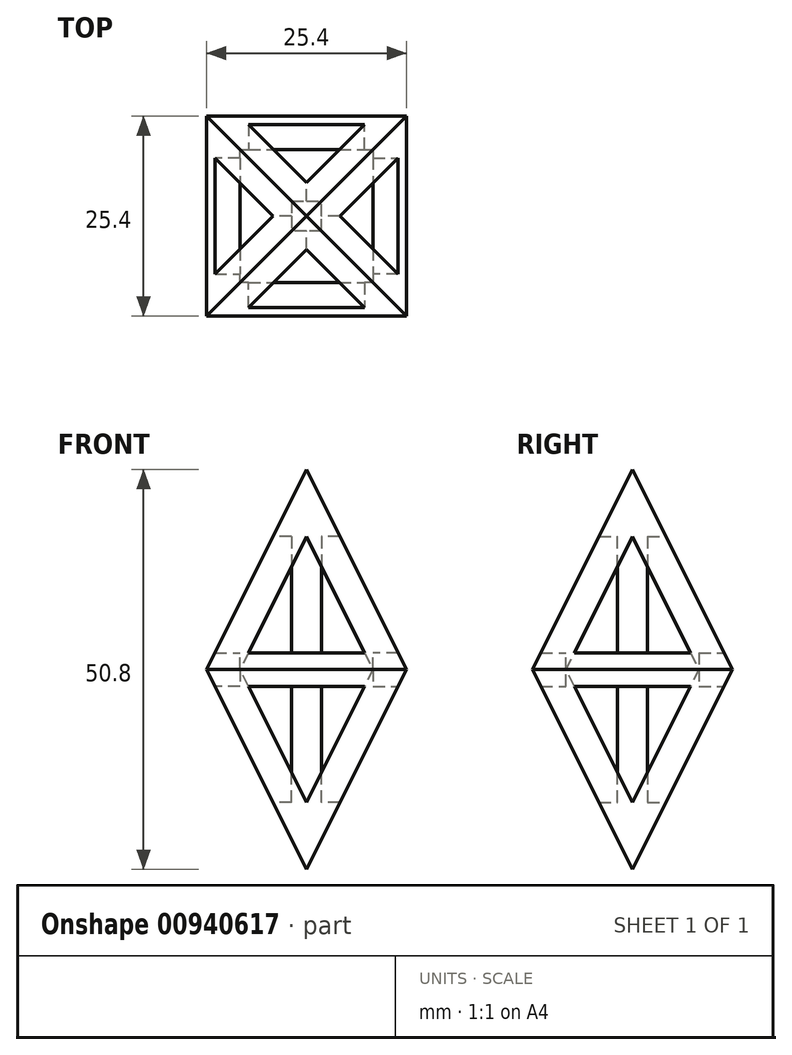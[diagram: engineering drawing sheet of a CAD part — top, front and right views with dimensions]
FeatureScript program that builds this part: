
annotation { "Feature Type Name" : "Feature", "Feature Type Description" : "" }
export const myFeature = defineFeature(function(context is Context, id is Id, definition is map)
    precondition{}
    {
        {
            var Q0;
            Q0=qCreatedBy(makeId("Right.planeOp"),FACE);
            var sketch = newSketch(context, id + "F0", { "sketchPlane" : qUnion([Q0])});
            skLineSegment(sketch, "E0.bottom", {"start": v(12.7, -25.4) * mm, "end": v(-12.7, -25.4) * mm});
            skLineSegment(sketch, "E0.top", {"start": v(12.7, 25.4) * mm, "end": v(-12.7, 25.4) * mm});
            skLineSegment(sketch, "E0.left", {"start": v(12.7, -25.4) * mm, "end": v(12.7, 25.4) * mm});
            skLineSegment(sketch, "E0.right", {"start": v(-12.7, -25.4) * mm, "end": v(-12.7, 25.4) * mm});
            skPoint(sketch, "E0.middle", {"position": v(0, 0) * mm});
            skSolve(sketch);
        }
        {
            var Q0;
            Q0=makeQuery(id+"F0.imprint","IMPRINT",FACE,{"disambiguationData":[TD([[makeQuery(id+"F0.imprint","IMPRINT",EDGE,{"derivedFrom":sQuery(id+"F0.wireOp",EDGE,"E0.bottom")}),-1.0]])]});
            extrude(context, id + "F1", {"entities" : qUnion([Q0]), "depth" : 25.4 * mm, "offsetDistance" : 25.4 * mm});
        }
        {
            var Q0;
            Q0=makeQuery(id+"F1.opExtrude","CAP_FACE",FACE,{"disambiguationData":[OSD([sQuery(id+"F0.wireOp",EDGE,"E0.bottom"),sQuery(id+"F0.wireOp",EDGE,"E0.top"),sQuery(id+"F0.wireOp",EDGE,"E0.left"),sQuery(id+"F0.wireOp",EDGE,"E0.right")])],"isStart":true});
            var sketch = newSketch(context, id + "F2", { "sketchPlane" : qUnion([Q0])});
            skLineSegment(sketch, "E1", {"start": v(0, 25.4) * mm, "end": v(-12.7, 0) * mm});
            skLineSegment(sketch, "E2", {"start": v(-12.7, 0) * mm, "end": v(0, -25.4) * mm});
            skLineSegment(sketch, "E3", {"start": v(0, -25.4) * mm, "end": v(12.7, 0) * mm});
            skLineSegment(sketch, "E4", {"start": v(12.7, 0) * mm, "end": v(0, 25.4) * mm});
            skLineSegment(sketch, "E5", {"start": v(0, 16.88) * mm, "end": v(-8.44, 0) * mm});
            skLineSegment(sketch, "E6", {"start": v(-8.44, 0) * mm, "end": v(0, -16.88) * mm});
            skLineSegment(sketch, "E7", {"start": v(0, -16.88) * mm, "end": v(8.44, 0) * mm});
            skLineSegment(sketch, "E8", {"start": v(8.44, 0) * mm, "end": v(0, 16.88) * mm});
            skSolve(sketch);
        }
        {
            var Q0;
            Q0=makeQuery(id+"F1.opExtrude","SWEPT_FACE",FACE,{"disambiguationData":[OSD([sQuery(id+"F0.wireOp",EDGE,"E0.left")])]});
            var sketch = newSketch(context, id + "F3", { "sketchPlane" : qUnion([Q0])});
            skLineSegment(sketch, "E9", {"start": v(-12.7, 25.4) * mm, "end": v(-25.4, 0) * mm});
            skLineSegment(sketch, "E10", {"start": v(-25.4, 0) * mm, "end": v(-12.7, -25.4) * mm});
            skLineSegment(sketch, "E11", {"start": v(-12.7, -25.4) * mm, "end": v(0, 0) * mm});
            skLineSegment(sketch, "E12", {"start": v(0, 0) * mm, "end": v(-12.7, 25.4) * mm});
            skLineSegment(sketch, "E13", {"start": v(-21.14, 0) * mm, "end": v(-12.7, 16.88) * mm});
            skLineSegment(sketch, "E14", {"start": v(-12.7, 16.88) * mm, "end": v(-4.26, 0) * mm});
            skLineSegment(sketch, "E15", {"start": v(-4.26, 0) * mm, "end": v(-12.7, -16.88) * mm});
            skLineSegment(sketch, "E16", {"start": v(-12.7, -16.88) * mm, "end": v(-21.14, 0) * mm});
            skSolve(sketch);
        }
        {
            var Q0;
            Q0=makeQuery(id+"F1.opExtrude","SWEPT_FACE",FACE,{"disambiguationData":[OSD([sQuery(id+"F0.wireOp",EDGE,"E0.bottom")])]});
            var sketch = newSketch(context, id + "F4", { "sketchPlane" : qUnion([Q0])});
            skLineSegment(sketch, "E17.bottom", {"start": v(10.8, 1.9) * mm, "end": v(14.6, 1.9) * mm});
            skLineSegment(sketch, "E17.top", {"start": v(10.8, -1.9) * mm, "end": v(14.6, -1.9) * mm});
            skLineSegment(sketch, "E17.left", {"start": v(10.8, 1.9) * mm, "end": v(10.8, -1.9) * mm});
            skLineSegment(sketch, "E17.right", {"start": v(14.6, 1.9) * mm, "end": v(14.6, -1.9) * mm});
            skPoint(sketch, "E17.middle", {"position": v(12.7, 0) * mm});
            skSolve(sketch);
        }
        {
            var Q0;
            Q0=makeQuery(id+"F2.imprint","IMPRINT",FACE,{"disambiguationData":[TD([[makeQuery(id+"F2.imprint","IMPRINT",EDGE,{"derivedFrom":sQuery(id+"F2.wireOp",EDGE,"E5")}),1.0]])]});
            extrude(context, id + "F5", {"entities" : qUnion([Q0]), "operationType" : NewBodyOperationType.REMOVE, "oppositeDirection" : true, "depth" : 25.4 * mm, "offsetDistance" : 25.4 * mm});
        }
        {
            var Q0;
            Q0=makeQuery(id+"F3.imprint","IMPRINT",FACE,{"disambiguationData":[TD([[makeQuery(id+"F3.imprint","IMPRINT",EDGE,{"derivedFrom":sQuery(id+"F3.wireOp",EDGE,"E13")}),-1.0]])]});
            extrude(context, id + "F6", {"entities" : qUnion([Q0]), "operationType" : NewBodyOperationType.REMOVE, "oppositeDirection" : true, "depth" : 25.4 * mm, "offsetDistance" : 25.4 * mm});
        }
        {
            var Q0;
            Q0=makeQuery(id+"F4.imprint","IMPRINT",FACE,{"disambiguationData":[TD([[makeQuery(id+"F4.imprint","IMPRINT",EDGE,{"derivedFrom":sQuery(id+"F4.wireOp",EDGE,"E17.bottom")}),-1.0]])]});
            extrude(context, id + "F7", {"entities" : qUnion([Q0]), "operationType" : NewBodyOperationType.ADD, "oppositeDirection" : true, "depth" : 50.8 * mm, "offsetDistance" : 25.4 * mm});
        }
        {
            var Q0;
            Q0=makeQuery(id+"F1.opExtrude","CAP_FACE",FACE,{"disambiguationData":[OSD([sQuery(id+"F0.wireOp",EDGE,"E0.bottom"),sQuery(id+"F0.wireOp",EDGE,"E0.top"),sQuery(id+"F0.wireOp",EDGE,"E0.left"),sQuery(id+"F0.wireOp",EDGE,"E0.right")])],"isStart":false});
            var sketch = newSketch(context, id + "F8", { "sketchPlane" : qUnion([Q0])});
            skLineSegment(sketch, "E18.bottom", {"start": v(-12.7, -2.13) * mm, "end": v(-8.44, -2.13) * mm});
            skLineSegment(sketch, "E18.top", {"start": v(-12.7, 2.13) * mm, "end": v(-8.44, 2.13) * mm});
            skLineSegment(sketch, "E18.left", {"start": v(-12.7, -2.13) * mm, "end": v(-12.7, 2.13) * mm});
            skLineSegment(sketch, "E18.right", {"start": v(-8.44, -2.13) * mm, "end": v(-8.44, 2.13) * mm});
            skPoint(sketch, "E19.firstSnap0", {"position": v(-10.57, -2.13) * mm});
            skLineSegment(sketch, "E19.bottom", {"start": v(12.7, -2.13) * mm, "end": v(8.44, -2.13) * mm});
            skLineSegment(sketch, "E19.top", {"start": v(12.7, 2.13) * mm, "end": v(8.44, 2.13) * mm});
            skLineSegment(sketch, "E19.left", {"start": v(12.7, -2.13) * mm, "end": v(12.7, 2.13) * mm});
            skLineSegment(sketch, "E19.right", {"start": v(8.44, -2.13) * mm, "end": v(8.44, 2.13) * mm});
            skSolve(sketch);
        }
        {
            var Q0;
            {var subQ2=sQuery(id+"F8.wireOp",EDGE,"E18.bottom");Q0=makeQuery(id+"F8.imprint","IMPRINT",FACE,{"disambiguationData":[TD([[makeQuery(id+"F8.imprint","IMPRINT",EDGE,{"derivedFrom":subQ2}),1.0]])]});}
            var Q1;
            {var subQ2=sQuery(id+"F8.wireOp",EDGE,"E19.bottom");Q1=makeQuery(id+"F8.imprint","IMPRINT",FACE,{"disambiguationData":[TD([[makeQuery(id+"F8.imprint","IMPRINT",EDGE,{"derivedFrom":subQ2}),-1.0]])]});}
            extrude(context, id + "F9", {"entities" : qUnion([Q0, Q1]), "operationType" : NewBodyOperationType.ADD, "oppositeDirection" : true, "depth" : 25.4 * mm, "offsetDistance" : 25.4 * mm});
        }
        {
            var Q0;
            Q0=makeQuery(id+"F9.boolean.opBoolean","MERGE",FACE,{"derivedFrom":[makeQuery(id+"F1.opExtrude","SWEPT_FACE",FACE,{"disambiguationData":[OSD([sQuery(id+"F0.wireOp",EDGE,"E0.right")])]}),makeQuery(id+"F9.opExtrude","SWEPT_FACE",FACE,{"disambiguationData":[OSD([sQuery(id+"F8.wireOp",EDGE,"E18.left")])]})]});
            var sketch = newSketch(context, id + "F10", { "sketchPlane" : qUnion([Q0])});
            skLineSegment(sketch, "E20.bottom", {"start": v(0, -2.13) * mm, "end": v(4.26, -2.13) * mm});
            skLineSegment(sketch, "E20.top", {"start": v(0, 2.13) * mm, "end": v(4.26, 2.13) * mm});
            skLineSegment(sketch, "E20.left", {"start": v(0, -2.13) * mm, "end": v(0, 2.13) * mm});
            skLineSegment(sketch, "E20.right", {"start": v(4.26, -2.13) * mm, "end": v(4.26, 2.13) * mm});
            skLineSegment(sketch, "E21.bottom", {"start": v(25.4, -2.13) * mm, "end": v(21.14, -2.13) * mm});
            skLineSegment(sketch, "E21.top", {"start": v(25.4, 2.13) * mm, "end": v(21.14, 2.13) * mm});
            skLineSegment(sketch, "E21.left", {"start": v(25.4, -2.13) * mm, "end": v(25.4, 2.13) * mm});
            skLineSegment(sketch, "E21.right", {"start": v(21.14, -2.13) * mm, "end": v(21.14, 2.13) * mm});
            skSolve(sketch);
        }
        {
            var Q0;
            Q0=makeQuery(id+"F10.imprint","IMPRINT",FACE,{"disambiguationData":[TD([[makeQuery(id+"F10.imprint","IMPRINT",EDGE,{"derivedFrom":sQuery(id+"F10.wireOp",EDGE,"E20.bottom")}),1.0]])]});
            var Q1;
            Q1=makeQuery(id+"F10.imprint","IMPRINT",FACE,{"disambiguationData":[TD([[makeQuery(id+"F10.imprint","IMPRINT",EDGE,{"derivedFrom":sQuery(id+"F10.wireOp",EDGE,"E21.bottom")}),-1.0]])]});
            extrude(context, id + "F11", {"entities" : qUnion([Q0, Q1]), "operationType" : NewBodyOperationType.ADD, "oppositeDirection" : true, "depth" : 25.4 * mm, "offsetDistance" : 25.4 * mm});
        }
        {
            var Q0;
            {var subQ0=sQuery(id+"F3.wireOp",EDGE,"E12");Q0=makeQuery(id+"F3.imprint","IMPRINT",FACE,{"disambiguationData":[TD([[makeQuery(id+"F3.imprint","IMPRINT",EDGE,{"derivedFrom":subQ0}),-1.0]])]});}
            var Q1;
            {var subQ0=sQuery(id+"F3.wireOp",EDGE,"E9");Q1=makeQuery(id+"F3.imprint","IMPRINT",FACE,{"disambiguationData":[TD([[makeQuery(id+"F3.imprint","IMPRINT",EDGE,{"derivedFrom":subQ0}),-1.0]])]});}
            var Q2;
            {var subQ0=sQuery(id+"F3.wireOp",EDGE,"E10");Q2=makeQuery(id+"F3.imprint","IMPRINT",FACE,{"disambiguationData":[TD([[makeQuery(id+"F3.imprint","IMPRINT",EDGE,{"derivedFrom":subQ0}),-1.0]])]});}
            var Q3;
            {var subQ0=sQuery(id+"F3.wireOp",EDGE,"E11");Q3=makeQuery(id+"F3.imprint","IMPRINT",FACE,{"disambiguationData":[TD([[makeQuery(id+"F3.imprint","IMPRINT",EDGE,{"derivedFrom":subQ0}),-1.0]])]});}
            extrude(context, id + "F12", {"entities" : qUnion([Q0, Q1, Q2, Q3]), "operationType" : NewBodyOperationType.REMOVE, "oppositeDirection" : true, "depth" : 25.4 * mm, "offsetDistance" : 25.4 * mm});
        }
        {
            var Q0;
            {var subQ0=sQuery(id+"F2.wireOp",EDGE,"E1");Q0=makeQuery(id+"F2.imprint","IMPRINT",FACE,{"disambiguationData":[TD([[makeQuery(id+"F2.imprint","IMPRINT",EDGE,{"derivedFrom":subQ0}),-1.0]])]});}
            var Q1;
            {var subQ0=sQuery(id+"F2.wireOp",EDGE,"E4");Q1=makeQuery(id+"F2.imprint","IMPRINT",FACE,{"disambiguationData":[TD([[makeQuery(id+"F2.imprint","IMPRINT",EDGE,{"derivedFrom":subQ0}),-1.0]])]});}
            var Q2;
            {var subQ0=sQuery(id+"F2.wireOp",EDGE,"E3");Q2=makeQuery(id+"F2.imprint","IMPRINT",FACE,{"disambiguationData":[TD([[makeQuery(id+"F2.imprint","IMPRINT",EDGE,{"derivedFrom":subQ0}),-1.0]])]});}
            var Q3;
            {var subQ0=sQuery(id+"F2.wireOp",EDGE,"E2");Q3=makeQuery(id+"F2.imprint","IMPRINT",FACE,{"disambiguationData":[TD([[makeQuery(id+"F2.imprint","IMPRINT",EDGE,{"derivedFrom":subQ0}),-1.0]])]});}
            extrude(context, id + "F13", {"entities" : qUnion([Q0, Q1, Q2, Q3]), "operationType" : NewBodyOperationType.REMOVE, "oppositeDirection" : true, "depth" : 25.4 * mm, "offsetDistance" : 25.4 * mm});
        }
    });
